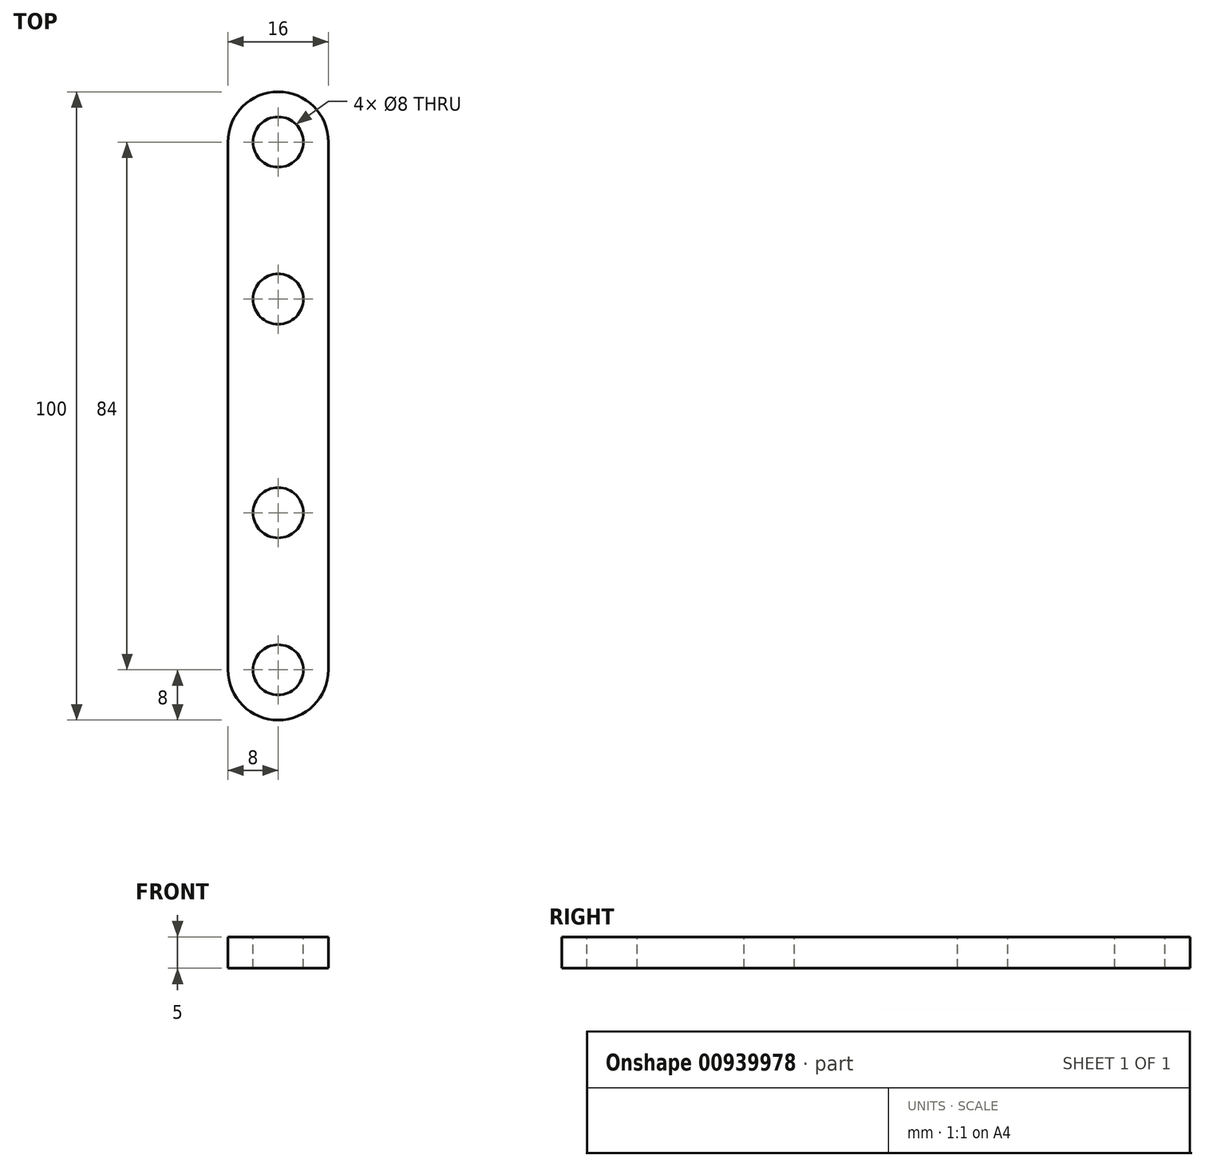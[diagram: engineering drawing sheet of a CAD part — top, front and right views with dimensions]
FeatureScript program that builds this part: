
annotation { "Feature Type Name" : "Feature", "Feature Type Description" : "" }
export const myFeature = defineFeature(function(context is Context, id is Id, definition is map)
    precondition{}
    {
        {
            var Q0;
            Q0=qCreatedBy(makeId("Top.planeOp"),FACE);
            var sketch = newSketch(context, id + "F0", { "sketchPlane" : qUnion([Q0])});
            skLineSegment(sketch, "E0.bottom", {"start": v(0, 0) * mm, "end": v(16, 0) * mm});
            skLineSegment(sketch, "E0.top", {"start": v(0, 100) * mm, "end": v(16, 100) * mm});
            skLineSegment(sketch, "E0.left", {"start": v(0, 0) * mm, "end": v(0, 100) * mm});
            skLineSegment(sketch, "E0.right", {"start": v(16, 0) * mm, "end": v(16, 100) * mm});
            skSolve(sketch);
        }
        {
            var Q0;
            Q0=makeQuery(id+"F0.imprint","IMPRINT",FACE,{"disambiguationData":[TD([[makeQuery(id+"F0.imprint","IMPRINT",EDGE,{"derivedFrom":sQuery(id+"F0.wireOp",EDGE,"E0.bottom")}),1.0]])]});
            extrude(context, id + "F1", {"entities" : qUnion([Q0]), "depth" : 5 * mm, "offsetDistance" : 25 * mm});
        }
        {
            var Q0;
            Q0=makeQuery(id+"F1.opExtrude","SWEPT_EDGE",EDGE,{"disambiguationData":[OSD([sQuery(id+"F0.wireOp",EDGE,"E0.bottom"),sQuery(id+"F0.wireOp",EDGE,"E0.right")])]});
            var Q1;
            Q1=makeQuery(id+"F1.opExtrude","SWEPT_EDGE",EDGE,{"disambiguationData":[OSD([sQuery(id+"F0.wireOp",EDGE,"E0.bottom"),sQuery(id+"F0.wireOp",EDGE,"E0.left")])]});
            var Q2;
            Q2=makeQuery(id+"F1.opExtrude","SWEPT_EDGE",EDGE,{"disambiguationData":[OSD([sQuery(id+"F0.wireOp",EDGE,"E0.top"),sQuery(id+"F0.wireOp",EDGE,"E0.right")])]});
            var Q3;
            Q3=makeQuery(id+"F1.opExtrude","SWEPT_EDGE",EDGE,{"disambiguationData":[OSD([sQuery(id+"F0.wireOp",EDGE,"E0.top"),sQuery(id+"F0.wireOp",EDGE,"E0.left")])]});
            fillet(context, id + "F2", {"entities" : qUnion([Q0, Q1, Q2, Q3]), "radius" : 8 * mm, "tangentPropagation" : true, "allowEdgeOverflow" : false});
        }
        {
            var Q0;
            Q0=makeQuery(id+"F1.opExtrude","CAP_FACE",FACE,{"disambiguationData":[OSD([sQuery(id+"F0.wireOp",EDGE,"E0.bottom"),sQuery(id+"F0.wireOp",EDGE,"E0.top"),sQuery(id+"F0.wireOp",EDGE,"E0.left"),sQuery(id+"F0.wireOp",EDGE,"E0.right")])],"isStart":false});
            var sketch = newSketch(context, id + "F3", { "sketchPlane" : qUnion([Q0])});
            skPoint(sketch, "E1", {"position": v(8, 8) * mm});
            skPoint(sketch, "E2", {"position": v(8, 92) * mm});
            skPoint(sketch, "E3", {"position": v(8, 67) * mm});
            skPoint(sketch, "E4", {"position": v(8, 33) * mm});
            skSolve(sketch);
        }
        {
            var Q0;
            Q0=sQuery(id+"F3.wireOp",VERTEX,"E2");
            var Q1;
            Q1=sQuery(id+"F3.wireOp",VERTEX,"E3");
            var Q2;
            Q2=sQuery(id+"F3.wireOp",VERTEX,"E4");
            var Q3;
            Q3=sQuery(id+"F3.wireOp",VERTEX,"E1");
            var Q4;
            Q4=makeQuery(id+"F1.opExtrude","SWEPT_BODY",BODY,{"disambiguationData":[OSD([sQuery(id+"F0.wireOp",EDGE,"E0.bottom"),sQuery(id+"F0.wireOp",EDGE,"E0.top"),sQuery(id+"F0.wireOp",EDGE,"E0.left"),sQuery(id+"F0.wireOp",EDGE,"E0.right")])]});
            hole(context, id + "F4", {"style" : HoleStyle.SIMPLE, "endStyle" : HoleEndStyle.THROUGH, "holeDiameter" : 8 * mm, "majorDiameter" : 5 * mm, "isTappedThrough" : true, "tappedDepth" : 12 * mm, "tapClearance" : 3, "locations" : qUnion([Q0, Q1, Q2, Q3]), "scope" : qUnion([Q4])});
        }
    });
